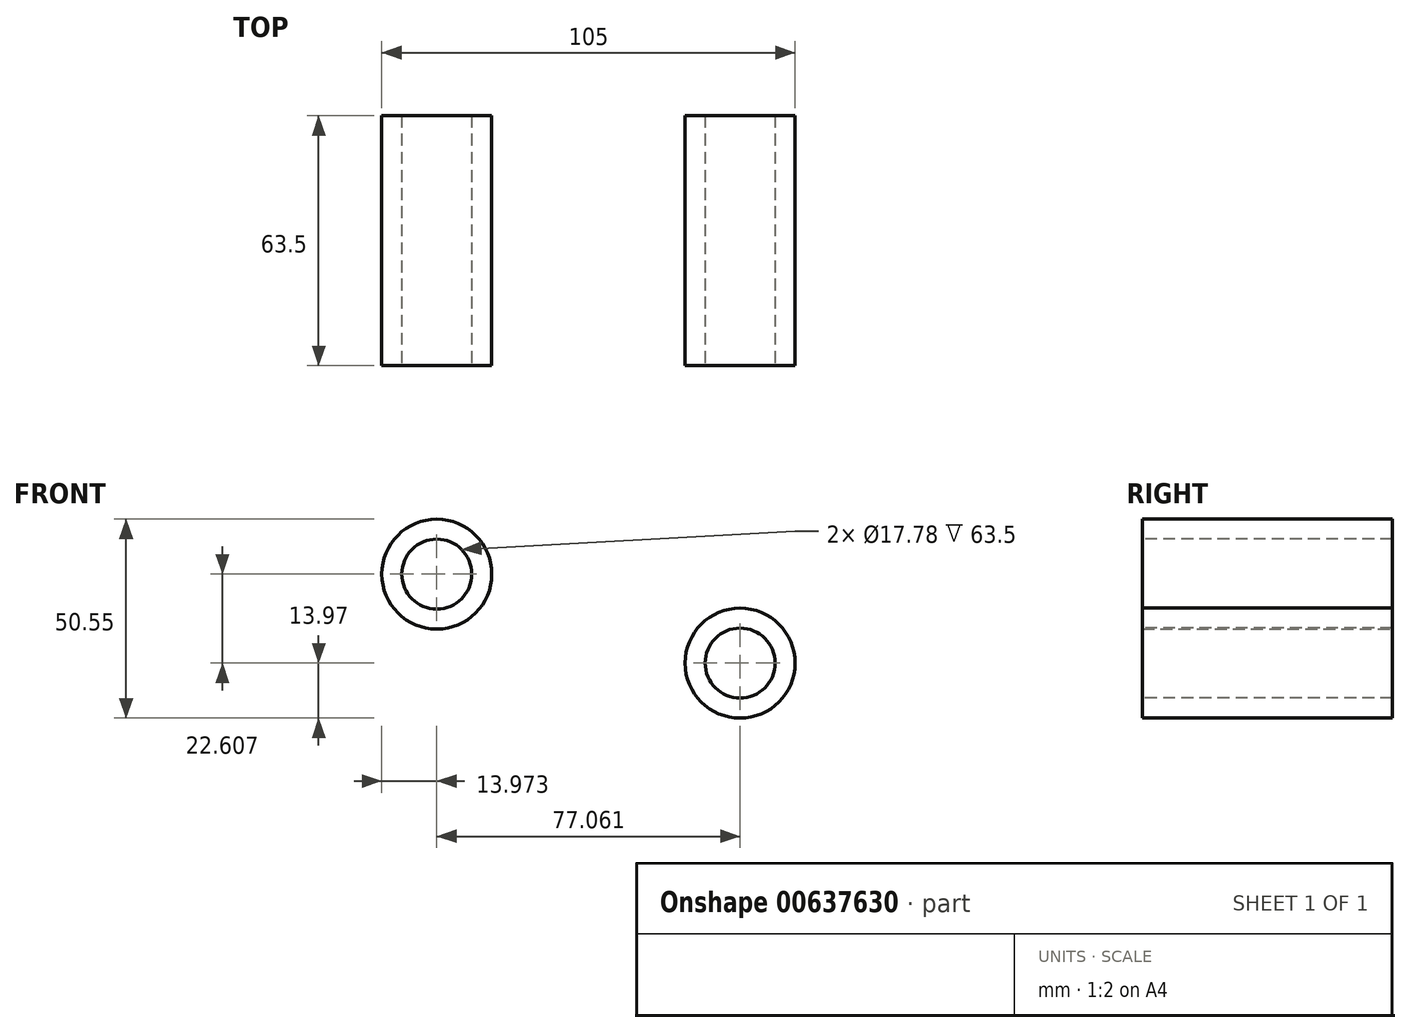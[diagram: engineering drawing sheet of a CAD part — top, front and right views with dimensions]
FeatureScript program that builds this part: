
annotation { "Feature Type Name" : "Feature", "Feature Type Description" : "" }
export const myFeature = defineFeature(function(context is Context, id is Id, definition is map)
    precondition{}
    {
        {
            var Q0;
            Q0=qCreatedBy(makeId("Front.planeOp"),FACE);
            var sketch = newSketch(context, id + "F0", { "sketchPlane" : qUnion([Q0])});
            skCircle(sketch, "E0", {"center": v(-59.47, 42.17) * mm, "radius": 13.97 * mm});
            skCircle(sketch, "E1", {"center": v(17.6, 19.56) * mm, "radius": 13.97 * mm});
            skSolve(sketch);
        }
        {
            var Q0;
            Q0 = qSketchRegion(id + "F0", true);
            extrude(context, id + "F1", {"entities" : qUnion([Q0]), "depth" : 63.5 * mm, "offsetDistance" : 25.4 * mm});
        }
        {
            var Q0;
            Q0=makeQuery(id+"F1.opExtrude","CAP_FACE",FACE,{"disambiguationData":[OSD([sQuery(id+"F0.wireOp",EDGE,"E0")])],"isStart":false});
            var sketch = newSketch(context, id + "F2", { "sketchPlane" : qUnion([Q0])});
            skCircle(sketch, "E2", {"center": v(-59.47, 42.17) * mm, "radius": 8.9 * mm});
            skSolve(sketch);
        }
        {
            var Q0;
            Q0=makeQuery(id+"F2.imprint","IMPRINT",FACE,{"disambiguationData":[TD([[makeQuery(id+"F2.imprint","IMPRINT",EDGE,{"derivedFrom":sQuery(id+"F2.wireOp",EDGE,"E2")}),1.0]])]});
            extrude(context, id + "F3", {"entities" : qUnion([Q0]), "operationType" : NewBodyOperationType.REMOVE, "oppositeDirection" : true, "depth" : 63.5 * mm, "offsetDistance" : 25.4 * mm});
        }
        {
            var Q0;
            Q0=makeQuery(id+"F1.opExtrude","CAP_FACE",FACE,{"disambiguationData":[OSD([sQuery(id+"F0.wireOp",EDGE,"E1")])],"isStart":false});
            var sketch = newSketch(context, id + "F4", { "sketchPlane" : qUnion([Q0])});
            skCircle(sketch, "E3", {"center": v(17.6, 19.56) * mm, "radius": 8.9 * mm});
            skSolve(sketch);
        }
        {
            var Q0;
            Q0=makeQuery(id+"F4.imprint","IMPRINT",FACE,{"disambiguationData":[TD([[makeQuery(id+"F4.imprint","IMPRINT",EDGE,{"derivedFrom":sQuery(id+"F4.wireOp",EDGE,"E3")}),1.0]])]});
            extrude(context, id + "F5", {"entities" : qUnion([Q0]), "operationType" : NewBodyOperationType.REMOVE, "oppositeDirection" : true, "depth" : 63.5 * mm, "offsetDistance" : 25.4 * mm});
        }
    });
